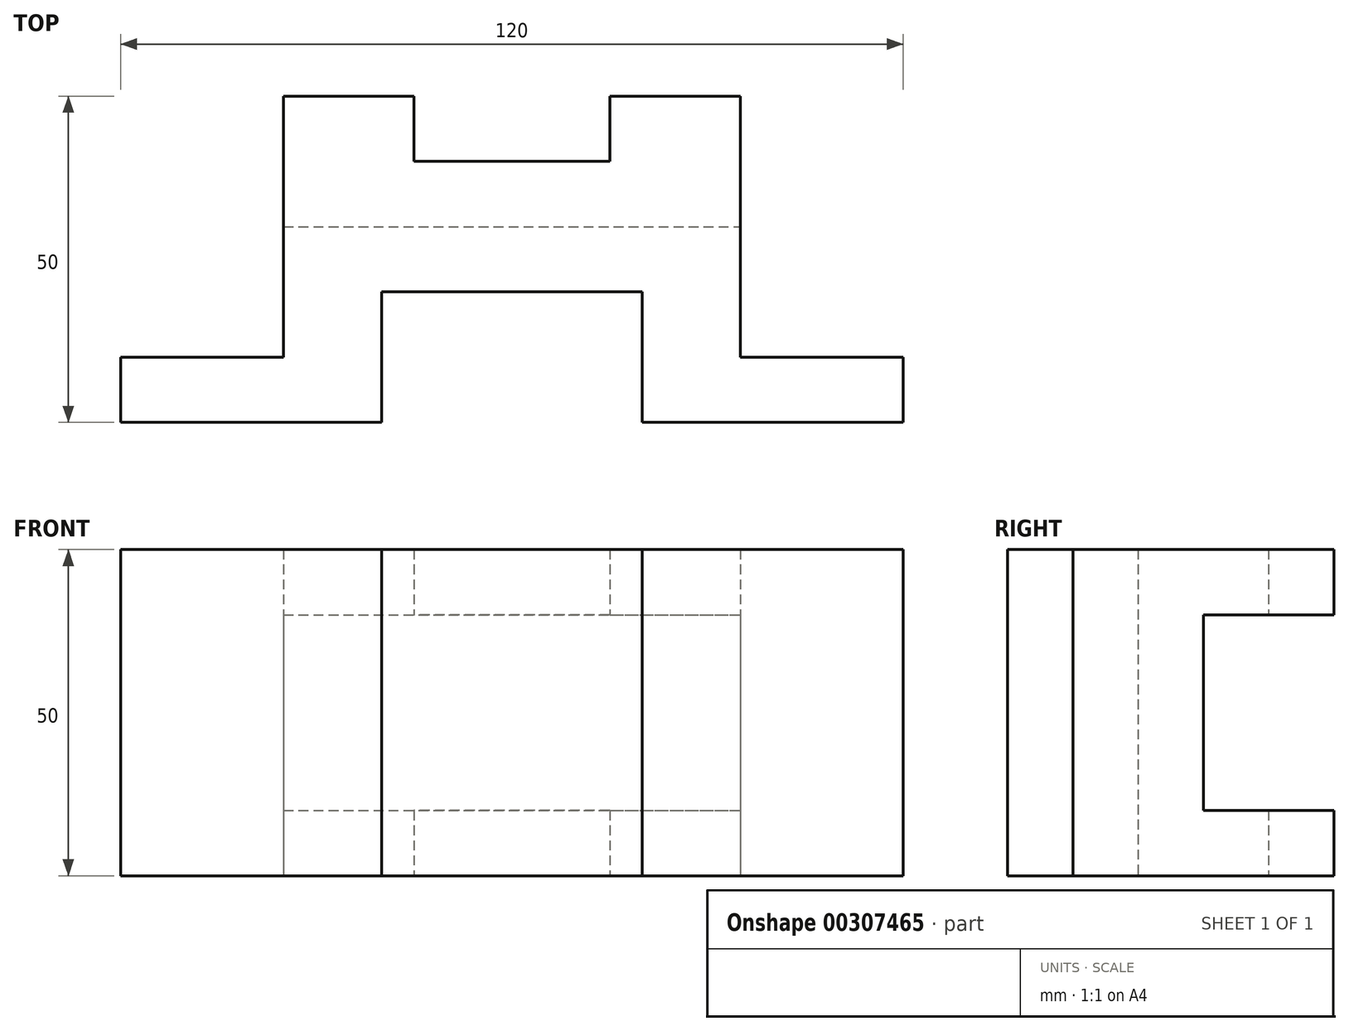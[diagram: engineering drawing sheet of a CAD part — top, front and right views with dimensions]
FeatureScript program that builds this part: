
annotation { "Feature Type Name" : "Feature", "Feature Type Description" : "" }
export const myFeature = defineFeature(function(context is Context, id is Id, definition is map)
    precondition{}
    {
        {
            assignVariable(context, id + "F0", {"name" : "A", "anyValue" : 50});
        }
        {
            var Q0;
            Q0=qCreatedBy(makeId("Top.planeOp"),FACE);
            var sketch = newSketch(context, id + "F1", { "sketchPlane" : qUnion([Q0])});
            skLineSegment(sketch, "E0", {"start": v(0, 0) * mm, "end": v(40, 0) * mm});
            skLineSegment(sketch, "E1", {"start": v(40, 0) * mm, "end": v(40, 20) * mm});
            skLineSegment(sketch, "E2", {"start": v(40, 20) * mm, "end": v(80, 20) * mm});
            skLineSegment(sketch, "E3", {"start": v(80, 20) * mm, "end": v(80, 0) * mm});
            skLineSegment(sketch, "E4", {"start": v(80, 0) * mm, "end": v(120, 0) * mm});
            skLineSegment(sketch, "E5", {"start": v(120, 0) * mm, "end": v(120, 10) * mm});
            skLineSegment(sketch, "E6", {"start": v(120, 10) * mm, "end": v(95, 10) * mm});
            skLineSegment(sketch, "E7", {"start": v(95, 10) * mm, "end": v(95, 50) * mm});
            skLineSegment(sketch, "E8", {"start": v(95, 50) * mm, "end": v(75, 50) * mm});
            skLineSegment(sketch, "E9", {"start": v(75, 50) * mm, "end": v(75, 40) * mm});
            skLineSegment(sketch, "E10", {"start": v(75, 40) * mm, "end": v(45, 40) * mm});
            skLineSegment(sketch, "E11", {"start": v(45, 40) * mm, "end": v(45, 50) * mm});
            skLineSegment(sketch, "E12", {"start": v(45, 50) * mm, "end": v(25, 50) * mm});
            skLineSegment(sketch, "E13", {"start": v(25, 50) * mm, "end": v(25, 10) * mm});
            skLineSegment(sketch, "E14", {"start": v(25, 10) * mm, "end": v(0, 10) * mm});
            skLineSegment(sketch, "E15", {"start": v(0, 10) * mm, "end": v(0, 0) * mm});
            skSolve(sketch);
        }
        {
            var Q0;
            Q0 = qSketchRegion(id + "F1", true);
            extrude(context, id + "F2", {"entities" : qUnion([Q0]), "depth" : (getVariable(context, 'A')) * mm});
        }
        {
            var Q0;
            Q0=makeQuery(id+"F2.opExtrude","SWEPT_FACE",FACE,{"disambiguationData":[OSD([sQuery(id+"F1.wireOp",EDGE,"E12")])]});
            var sketch = newSketch(context, id + "F3", { "sketchPlane" : qUnion([Q0])});
            skLineSegment(sketch, "E16.0", {"start": v(-95, 50) * mm, "end": v(-95, 0) * mm});
            skLineSegment(sketch, "E17.bottom", {"start": v(-25, 10) * mm, "end": v(-95, 10) * mm});
            skLineSegment(sketch, "E17.top", {"start": v(-25, 40) * mm, "end": v(-95, 40) * mm});
            skLineSegment(sketch, "E17.left", {"start": v(-25, 10) * mm, "end": v(-25, 40) * mm});
            skLineSegment(sketch, "E17.right", {"start": v(-95, 10) * mm, "end": v(-95, 40) * mm});
            skSolve(sketch);
        }
        {
            var Q0;
            Q0 = qSketchRegion(id + "F3", true);
            extrude(context, id + "F4", {"entities" : qUnion([Q0]), "operationType" : NewBodyOperationType.REMOVE, "oppositeDirection" : true, "depth" : 20 * mm});
        }
    });
